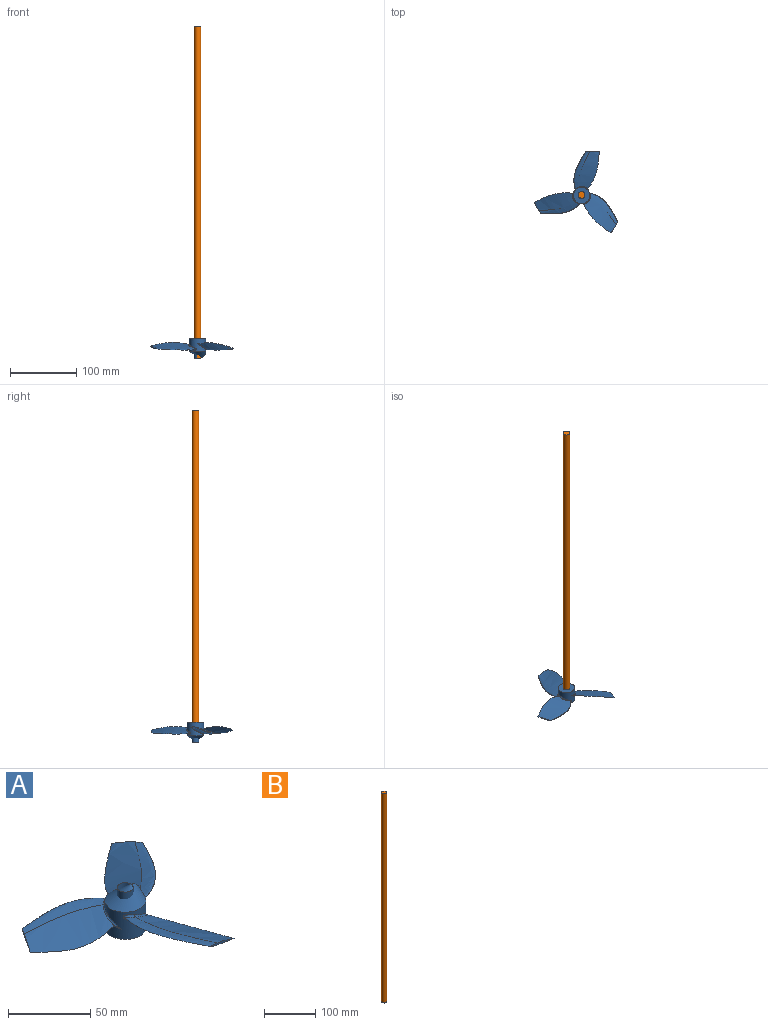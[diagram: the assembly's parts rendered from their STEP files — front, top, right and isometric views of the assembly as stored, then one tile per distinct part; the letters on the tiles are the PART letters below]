
ASSEMBLY  parts=2 mates=1
PART A: 19 faces, bbox 127.8x125.5x31.6 mm
  f0: cylinder r=12.5mm len=25mm, axis (0,0,-1), area 1390.9mm2, adj f1,f12,f13,f14,f15,f16,f17,f18
  f1: plane 25x25mm, normal (0,0,-1), area 412.3mm2, adj f0,f11
  f2: bspline ~73.51x30.51mm, area 1219.2mm2, adj f3,f4,f16,f17
  f3: bspline ~68.36x31.81mm, area 2053.8mm2, adj f2,f4,f16
  f4: plane 18.67x11.47mm, normal (-0.87,0.5,0), area 21.1mm2, adj f2,f3
  f5: bspline ~57.89x31.32mm, area 1219.2mm2, adj f6,f7,f14,f15
  f6: bspline ~67x42.86mm, area 2053.8mm2, adj f5,f7,f14
  f7: plane 21.3x5.8mm, normal (0,-1,0), area 21.1mm2, adj f5,f6
  f8: bspline ~56.04x48.91mm, area 1219.2mm2, adj f9,f10,f12,f13
  f9: bspline ~60.25x51.4mm, area 2053.8mm2, adj f8,f10,f12
  f10: plane 18.67x11.47mm, normal (0.87,0.5,0), area 21.1mm2, adj f8,f9
  f11: cylinder r=5mm len=30mm, axis (0,0,1), area 942.5mm2, adj f1,f18
  f12: bspline ~18.18x16.2mm, area 48.9mm2, adj f0,f8,f9,f13
  f13: bspline ~14.97x11.42mm, area 26.7mm2, adj f0,f8,f12
  f14: bspline ~22.71x11mm, area 48.9mm2, adj f0,f5,f6,f15
  f15: bspline ~16.87x11.42mm, area 26.7mm2, adj f0,f5,f14
  f16: bspline ~21.91x11.61mm, area 48.9mm2, adj f0,f2,f3,f17
  f17: bspline ~18.67x11.63mm, area 26.7mm2, adj f0,f2,f16
  f18: torus R=2.5mm, axis (0,0,1), area 815.4mm2, adj f0,f11
PART B: 3 faces, bbox 10x10x500 mm
  f0: cylinder r=5mm len=500mm, axis (0,0,-1), area 15708mm2, adj f1,f2
  f1: plane 10x10mm, normal (0,0,1), area 78.5mm2, adj f0
  f2: plane 10x10mm, normal (0,0,-1), area 78.5mm2, adj f0
PLACE A rot(axis=(1,0,0),180deg) t=(-4.44,0,15)mm
PLACE B at identity fixed
MATE fastened B.f0 <-> A.f0  axis (0,0,-1) through (0,0,0)mm
